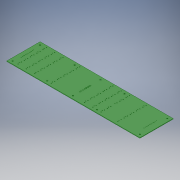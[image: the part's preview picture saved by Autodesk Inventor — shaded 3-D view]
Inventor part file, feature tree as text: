
AUTODESK INVENTOR PART (.ipt)
format: ipt  version: 2018 (Build 220112000, 112)  size: 4,278,272 bytes
history: native  units: in
note: dims shown in document units (in); Inventor stores cm internally (conversion verified against a paired STEP export)
features: sketch x3, extrude x2
ambient origin geometry x8: Origin, YZ Plane, XZ Plane, XY Plane, X Axis, Y Axis, Z Axis, Center Point
bodies: Solid1 (feature_tree)
feature tree (5):
  sketch  "Sketch3"  dims[d0=0.062in d1=0.0in d2=0.062in d3=0.0in]
  extrude  "Extrusion1"  Depth=0.062in TaperAngle=0.0deg
  extrude  "Extrusion2"  [1 undecoded]
  sketch  "Sketch4"
  sketch  "Sketch5"
note: 1 required parameter value undecoded (feature->parameter linkage not recoverable at this tier; creation-order binding heuristic only, values carry confidence <= 0.55)
